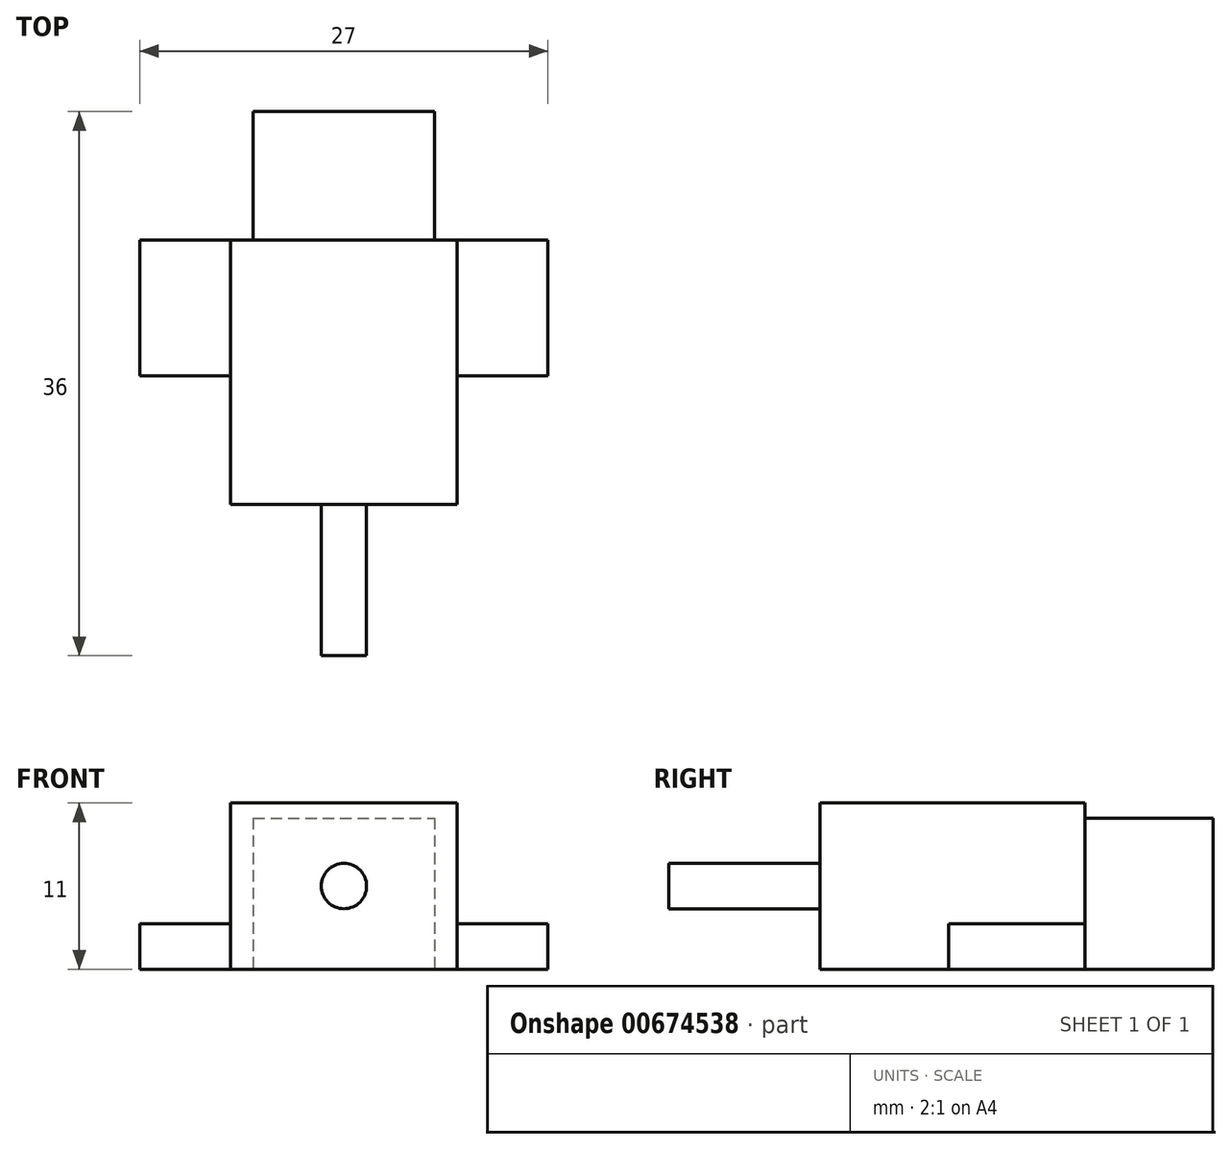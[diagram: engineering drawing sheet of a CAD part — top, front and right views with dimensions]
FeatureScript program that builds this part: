
annotation { "Feature Type Name" : "Feature", "Feature Type Description" : "" }
export const myFeature = defineFeature(function(context is Context, id is Id, definition is map)
    precondition{}
    {
        {
            var Q0;
            Q0=qCreatedBy(makeId("Top.planeOp"),FACE);
            var sketch = newSketch(context, id + "F0", { "sketchPlane" : qUnion([Q0])});
            skLineSegment(sketch, "E0.bottom", {"start": v(-6, 0) * mm, "end": v(6, 0) * mm});
            skLineSegment(sketch, "E0.top", {"start": v(-6, 26) * mm, "end": v(6, 26) * mm});
            skLineSegment(sketch, "E0.left", {"start": v(-6, 0) * mm, "end": v(-6, 26) * mm});
            skLineSegment(sketch, "E0.right", {"start": v(6, 0) * mm, "end": v(6, 26) * mm});
            skPoint(sketch, "E1", {"position": v(0, 0) * mm});
            skSolve(sketch);
        }
        {
            var Q0;
            Q0=makeQuery(id+"F0.imprint","IMPRINT",FACE,{"disambiguationData":[TD([[makeQuery(id+"F0.imprint","IMPRINT",EDGE,{"derivedFrom":sQuery(id+"F0.wireOp",EDGE,"E0.bottom")}),1.0]])]});
            extrude(context, id + "F1", {"entities" : qUnion([Q0]), "depth" : 10 * mm, "offsetDistance" : 25 * mm});
        }
        {
            var Q0;
            Q0=qCreatedBy(makeId("Top.planeOp"),FACE);
            var sketch = newSketch(context, id + "F2", { "sketchPlane" : qUnion([Q0])});
            skLineSegment(sketch, "E2.bottom", {"start": v(-7.5, 0) * mm, "end": v(7.5, 0) * mm});
            skLineSegment(sketch, "E2.top", {"start": v(-7.5, 17.5) * mm, "end": v(7.5, 17.5) * mm});
            skLineSegment(sketch, "E2.left", {"start": v(-7.5, 0) * mm, "end": v(-7.5, 17.5) * mm});
            skLineSegment(sketch, "E2.right", {"start": v(7.5, 0) * mm, "end": v(7.5, 17.5) * mm});
            skPoint(sketch, "E3", {"position": v(0, 0) * mm});
            skSolve(sketch);
        }
        {
            var Q0;
            Q0=makeQuery(id+"F2.imprint","IMPRINT",FACE,{"disambiguationData":[TD([[makeQuery(id+"F2.imprint","IMPRINT",EDGE,{"derivedFrom":sQuery(id+"F2.wireOp",EDGE,"E2.bottom")}),1.0]])]});
            extrude(context, id + "F3", {"entities" : qUnion([Q0]), "operationType" : NewBodyOperationType.ADD, "depth" : 11 * mm, "offsetDistance" : 25 * mm});
        }
        {
            var Q0;
            Q0=makeQuery(id+"F3.opExtrude","SWEPT_FACE",FACE,{"disambiguationData":[OSD([sQuery(id+"F2.wireOp",EDGE,"E2.right")])]});
            var sketch = newSketch(context, id + "F4", { "sketchPlane" : qUnion([Q0])});
            skLineSegment(sketch, "E4.bottom", {"start": v(17.5, 0) * mm, "end": v(8.5, 0) * mm});
            skLineSegment(sketch, "E4.top", {"start": v(17.5, 3) * mm, "end": v(8.5, 3) * mm});
            skLineSegment(sketch, "E4.left", {"start": v(17.5, 0) * mm, "end": v(17.5, 3) * mm});
            skLineSegment(sketch, "E4.right", {"start": v(8.5, 0) * mm, "end": v(8.5, 3) * mm});
            skSolve(sketch);
        }
        {
            var Q0;
            Q0=makeQuery(id+"F4.imprint","IMPRINT",FACE,{"disambiguationData":[TD([[makeQuery(id+"F4.imprint","IMPRINT",EDGE,{"derivedFrom":sQuery(id+"F4.wireOp",EDGE,"tTDc6Pnn-Xtcc-YM8V-wldO-8cZrUphgF9ss.bottom")}),1.0]])]});
            var Q1;
            Q1=makeQuery(id+"F4.imprint","IMPRINT",FACE,{"disambiguationData":[TD([[makeQuery(id+"F4.imprint","IMPRINT",EDGE,{"derivedFrom":sQuery(id+"F4.wireOp",EDGE,"E4.bottom")}),1.0]])]});
            extrude(context, id + "F5", {"entities" : qUnion([Q0, Q1]), "operationType" : NewBodyOperationType.ADD, "depth" : 6 * mm, "offsetDistance" : 25 * mm});
        }
        {
            var Q0;
            Q0=makeQuery(id+"F3.opExtrude","SWEPT_FACE",FACE,{"disambiguationData":[OSD([sQuery(id+"F2.wireOp",EDGE,"E2.left")])]});
            var sketch = newSketch(context, id + "F6", { "sketchPlane" : qUnion([Q0])});
            skLineSegment(sketch, "E5.bottom", {"start": v(-17.5, 0) * mm, "end": v(-8.5, 0) * mm});
            skLineSegment(sketch, "E5.top", {"start": v(-17.5, 3) * mm, "end": v(-8.5, 3) * mm});
            skLineSegment(sketch, "E5.left", {"start": v(-17.5, 0) * mm, "end": v(-17.5, 3) * mm});
            skLineSegment(sketch, "E5.right", {"start": v(-8.5, 0) * mm, "end": v(-8.5, 3) * mm});
            skSolve(sketch);
        }
        {
            var Q0;
            Q0=makeQuery(id+"F6.imprint","IMPRINT",FACE,{"disambiguationData":[TD([[makeQuery(id+"F6.imprint","IMPRINT",EDGE,{"derivedFrom":sQuery(id+"F6.wireOp",EDGE,"6B15RRWQ-SO7S-ZEXd-zUE4-YvTHLMvgojZ6.bottom")}),-1.0]])]});
            var Q1;
            Q1=makeQuery(id+"F6.imprint","IMPRINT",FACE,{"disambiguationData":[TD([[makeQuery(id+"F6.imprint","IMPRINT",EDGE,{"derivedFrom":sQuery(id+"F6.wireOp",EDGE,"E5.bottom")}),-1.0]])]});
            extrude(context, id + "F7", {"entities" : qUnion([Q0, Q1]), "operationType" : NewBodyOperationType.ADD, "depth" : 6 * mm, "offsetDistance" : 25 * mm});
        }
        {
            var Q0;
            Q0=makeQuery(id+"F3.boolean.opBoolean","MERGE",FACE,{"derivedFrom":[makeQuery(id+"F1.opExtrude","SWEPT_FACE",FACE,{"disambiguationData":[OSD([sQuery(id+"F0.wireOp",EDGE,"E0.bottom")])]}),makeQuery(id+"F3.opExtrude","SWEPT_FACE",FACE,{"disambiguationData":[OSD([sQuery(id+"F2.wireOp",EDGE,"E2.bottom")])]})]});
            var sketch = newSketch(context, id + "F8", { "sketchPlane" : qUnion([Q0])});
            skLineSegment(sketch, "E6", {"start": v(-7.5, 0) * mm, "end": v(7.5, 11) * mm, "construction": true});
            skLineSegment(sketch, "E7", {"start": v(-7.5, 11) * mm, "end": v(7.5, 0) * mm, "construction": true});
            skCircle(sketch, "E8", {"center": v(0, 5.5) * mm, "radius": 1.5 * mm});
            skSolve(sketch);
        }
        {
            var Q0;
            Q0=makeQuery(id+"F8.imprint","IMPRINT",FACE,{"disambiguationData":[TD([[makeQuery(id+"F8.imprint","IMPRINT",EDGE,{"derivedFrom":sQuery(id+"F8.wireOp",EDGE,"E8")}),1.0]])]});
            extrude(context, id + "F9", {"entities" : qUnion([Q0]), "operationType" : NewBodyOperationType.ADD, "depth" : 10 * mm, "offsetDistance" : 25 * mm});
        }
    });
